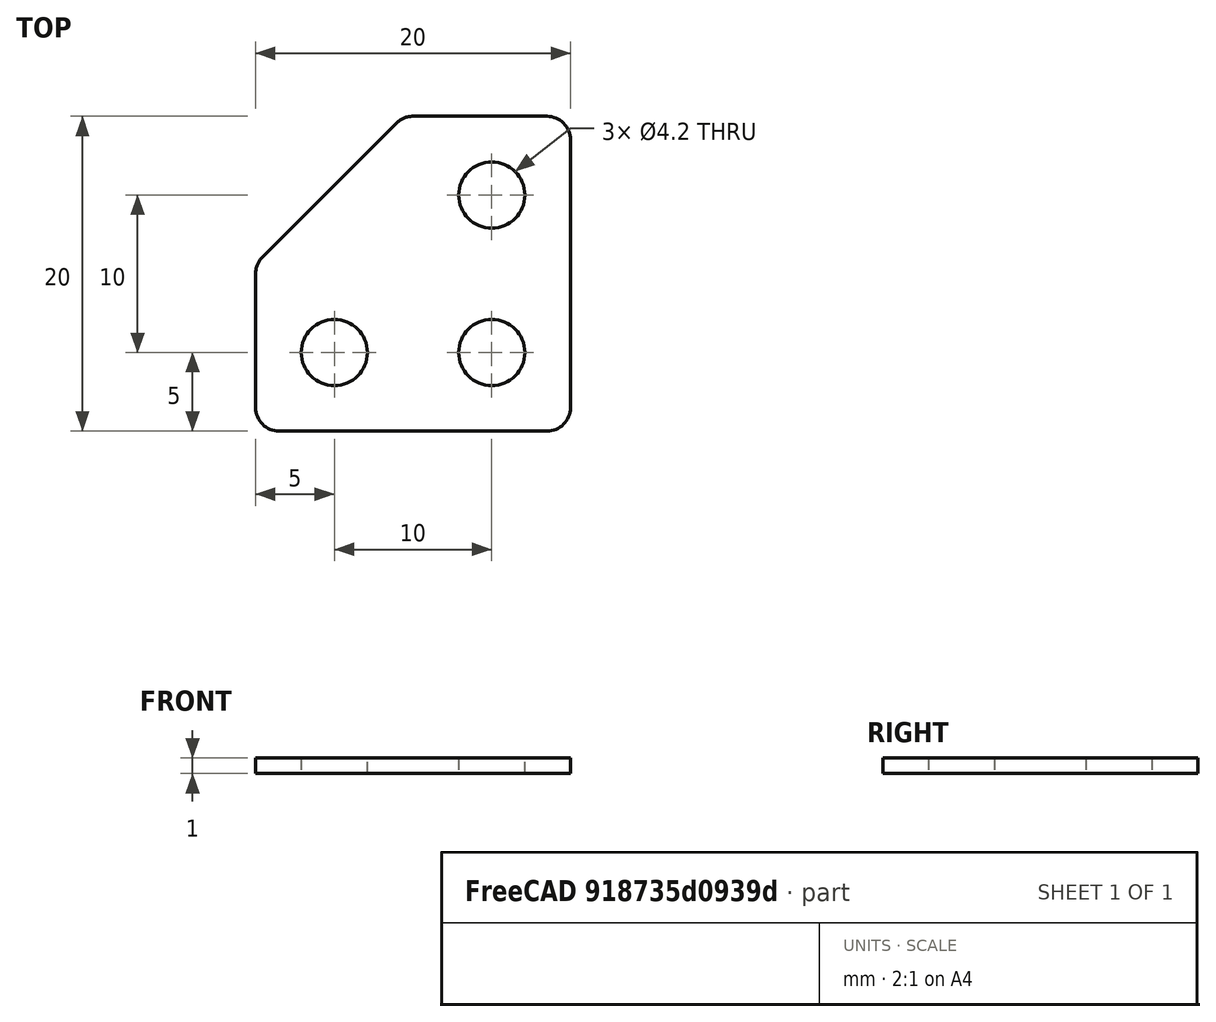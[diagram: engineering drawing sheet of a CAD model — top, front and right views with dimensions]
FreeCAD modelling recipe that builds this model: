
FCSTD DOCUMENT  (FreeCAD 0.16RUnknown)
Label: strip_2x2_corner
License: All rights reserved
LicenseURL: http://en.wikipedia.org/wiki/All_rights_reserved
objects: Drawing::FeatureViewPart×2, Sketcher::SketchObject×1, PartDesign::Pad×1, Drawing::FeaturePage×1
note: 3 computed .brp shape members not serialized (recipe doc carries the construction recipe); baked Part::Feature solids carry a one-line shape summary decoded from their .brp

FEATURE [Sketcher::SketchObject] Sketch
  sketch-geometry (13):
    g0: Circle CenterX=0 CenterY=10 CenterZ=0 NormalX=0 NormalY=0 NormalZ=1 Radius=2.1
    g1: Circle CenterX=-10 CenterY=0 CenterZ=0 NormalX=0 NormalY=0 NormalZ=1 Radius=2.1
    g2: Circle CenterX=0 CenterY=0 CenterZ=0 NormalX=0 NormalY=0 NormalZ=1 Radius=2.1
    g3: LineSegment StartX=-5 StartY=15 StartZ=0 EndX=3.5 EndY=15 EndZ=0
    g4: LineSegment StartX=5 StartY=13.5 StartZ=0 EndX=5 EndY=-3.5 EndZ=0
    g5: LineSegment StartX=3.5 StartY=-5 StartZ=0 EndX=-13.5 EndY=-5 EndZ=0
    g6: LineSegment StartX=-15 StartY=-3.5 StartZ=0 EndX=-15 EndY=5 EndZ=0
    g7: ArcOfCircle CenterX=3.5 CenterY=13.5 CenterZ=0 NormalX=0 NormalY=0 NormalZ=1 Radius=1.5 StartAngle=0 EndAngle=1.5708
    g8: ArcOfCircle CenterX=3.5 CenterY=-3.5 CenterZ=0 NormalX=0 NormalY=0 NormalZ=1 Radius=1.5 StartAngle=4.71239 EndAngle=6.28319
    g9: ArcOfCircle CenterX=-13.5 CenterY=-3.5 CenterZ=0 NormalX=0 NormalY=0 NormalZ=1 Radius=1.5 StartAngle=3.14159 EndAngle=4.71239
    g10: LineSegment StartX=-14.5607 StartY=6.06066 StartZ=0 EndX=-6.06066 EndY=14.5607 EndZ=0
    g11: ArcOfCircle CenterX=-5 CenterY=13.5 CenterZ=0 NormalX=0 NormalY=0 NormalZ=1 Radius=1.5 StartAngle=1.5708 EndAngle=2.35619
    g12: ArcOfCircle CenterX=-13.5 CenterY=5 CenterZ=0 NormalX=0 NormalY=0 NormalZ=1 Radius=1.5 StartAngle=2.35619 EndAngle=3.14159
  constraints (32):
    c: Distance(g-1,g1) = 10
    c: Distance(g-1,g0) = 10
    c: PointOnObject(g1,g-1)
    c: PointOnObject(g0,g-2)
    c: Horizontal(g3)
    c: Horizontal(g5)
    c: Vertical(g4)
    c: Vertical(g6)
    c: Tangent(g3,g7) = 1.5708
    c: Tangent(g4,g7) = 1.5708
    c: Tangent(g4,g8) = 1.5708
    c: Tangent(g5,g8) = 1.5708
    c: Tangent(g6,g9) = 1.5708
    c: Tangent(g5,g9) = 1.5708
    c: Equal(g1,g2)
    c: DistanceY(g5,g3) = 20
    c: Equal(g7,g9)
    c: Equal(g9,g8)
    c: DistanceX(g6,g1) = 5
    c: DistanceY(g5,g1) = 5
    c: Tangent(g10,g11) = 1.5708
    c: Tangent(g3,g11) = 1.5708
    c: Radius(g11) = 1.5
    c: Tangent(g10,g12) = 1.5708
    c: Tangent(g6,g12) = 1.5708
    c: Radius(g12) = 1.5
    c: DistanceX(g3,g4) = 10
    c: DistanceX(g0,g4) = 5
    c: DistanceY(g5,g6) = 10
    c: Radius(g7) = 1.5
    c: Radius(g0) = 2.1
    c: Equal(g0,g2)
FEATURE [PartDesign::Pad] Pad
  Length = 1
  Length2 = 100
  Sketch = -> Sketch
  Type = 0
FEATURE [Drawing::FeatureViewPart] Ortho  label="Ortho_0_0"
  Direction = (1,0,0)
  HiddenWidth = 0.15
  LineWidth = 0.35
  Rotation = -90
  ShowHiddenLines = false
  ShowSmoothLines = false
  Source = -> Pad
  Tolerance = 0.05
  ViewResult = <g id="Ortho_0_0"\n   transform="rotate(-90,100,250.5) translate(100,250.5) scale(1,1)"\n  >\n<g   stroke="rgb(0, 0, 0)"\n   stroke-width="0.35"\n   stroke-linecap="butt"\n   stroke-linejoin="miter"\n   fill="none"\n   transform="scale(1,-1)"\n  >\n<path id= "1" d=" M 0 -15 L 1 -15 " />\n<path d="M0,-13.5 L0,-13.6679  L0,-13.8338  L0,-13.9954  L0,-14.1508  L0,-14.298  L0,-14.4352  L0,-14.5607  L0,-14.6727  L0,-14.7701  L0,-14.8515  L0,-14.9158  L0,-14.9624  L0,-14.9906  L0,-15 " /><path d="M1,-13.5 L1,-13.6679  L1,-13.8338  L1,-13.9954  L1,-14.1508  L1,-14.298  L1,-14.4352  L1,-14.5607  L1,-14.6727  L1,-14.7701  L1,-14.8515  L1,-14.9158  L1,-14.9624  L1,-14.9906  L1,-15 " /><path id= "4" d=" M 0 -13.5 L 0 3.5 " />\n<path id= "5" d=" M 1 -13.5 L 1 3.5 " />\n<path id= "6" d=" M 0 5 L 1 5 " />\n<path d="M0,5 L0,4.99057  L0,4.96239  L0,4.91582  L0,4.85145  L0,4.77009  L0,4.67275  L0,4.56066  L0,4.43523  L0,4.29805  L0,4.15083  L0,3.99542  L0,3.83378  L0,3.66795  L0,3.5 " /><path d="M1,5 L1,4.99057  L1,4.96239  L1,4.91582  L1,4.85145  L1,4.77009  L1,4.67275  L1,4.56066  L1,4.43523  L1,4.29805  L1,4.15083  L1,3.99542  L1,3.83378  L1,3.66795  L1,3.5 " /></g>\n</g>
  Visible = true
  X = 100
  Y = 250.5
FEATURE [Drawing::FeatureViewPart] Ortho001  label="Ortho_0_1"
  Direction = (0,0,1)
  HiddenWidth = 0.15
  LineWidth = 0.35
  Rotation = 90
  ShowHiddenLines = false
  ShowSmoothLines = false
  Source = -> Pad
  Tolerance = 0.05
  ViewResult = <g id="Ortho_0_1"\n   transform="rotate(90,100,128) translate(100,128) scale(1,1)"\n  >\n<g   stroke="rgb(0, 0, 0)"\n   stroke-width="0.35"\n   stroke-linecap="butt"\n   stroke-linejoin="miter"\n   fill="none"\n   transform="scale(1,-1)"\n  >\n<path id= "1" d=" M -5 15 L 3.5 15 " />\n<path d="M5 13.5 A1.5 1.5 0 0 1 3.5 15" /><path id= "3" d=" M 5 13.5 L 5 -3.5 " />\n<path d="M3.5 -5 A1.5 1.5 0 0 1 5 -3.5" /><path id= "5" d=" M 3.5 -5 L -13.5 -5 " />\n<path d="M-15 -3.5 A1.5 1.5 0 0 1 -13.5 -5" /><path id= "7" d=" M -15 -3.5 L -15 5 " />\n<path d="M-14.5607 6.06066 A1.5 1.5 0 0 1 -15 5" /><path id= "9" d=" M -14.5607 6.06066 L -6.06066 14.5607 " />\n<path d="M-5 15 A1.5 1.5 0 0 1 -6.06066 14.5607" /><circle cx ="-10" cy ="0" r ="2.1" /><circle cx ="0" cy ="10" r ="2.1" /><circle cx ="0" cy ="0" r ="2.1" /></g>\n</g>
  Visible = true
  X = 100
  Y = 128
FEATURE [Drawing::FeaturePage] Page
  Group = -> [Ortho,Ortho001]
